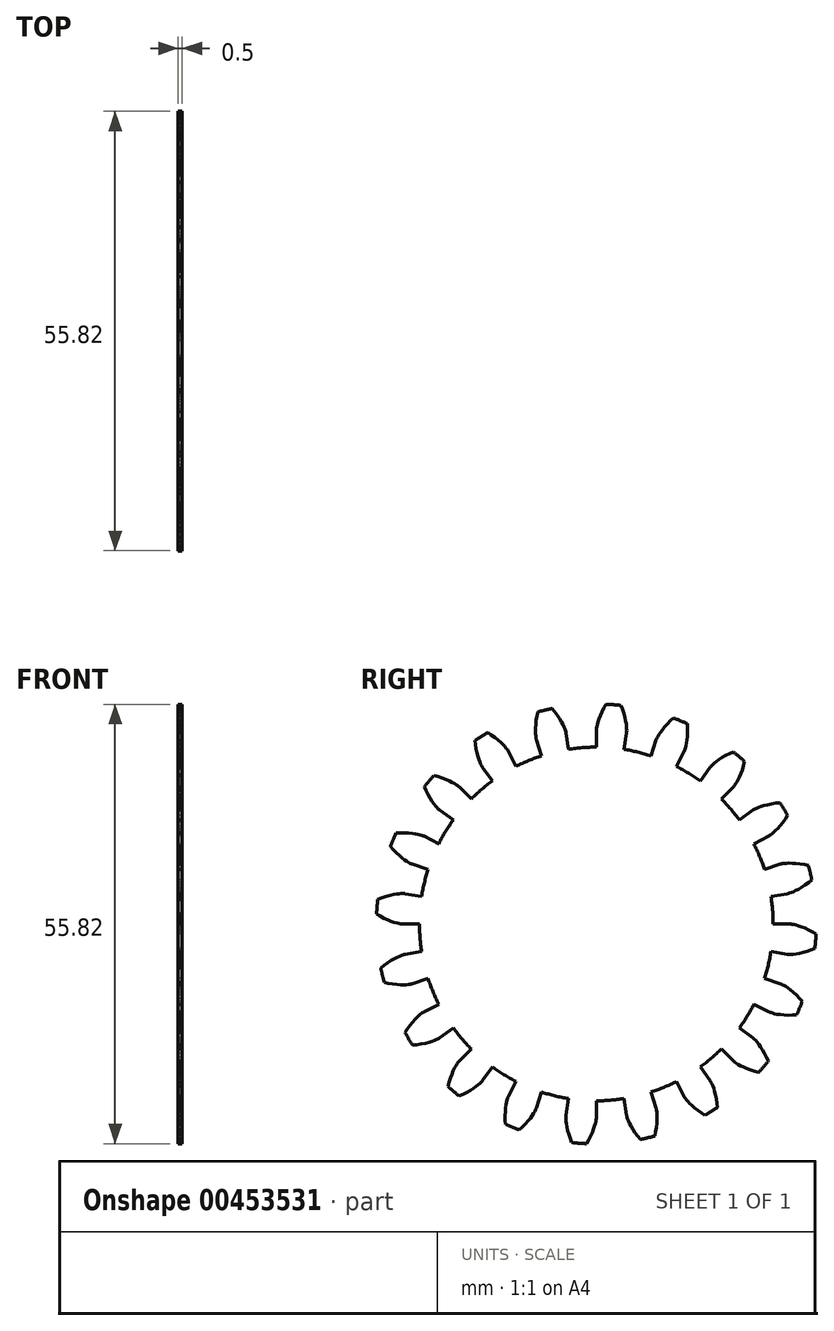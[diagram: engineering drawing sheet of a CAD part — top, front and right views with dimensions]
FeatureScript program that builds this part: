
annotation { "Feature Type Name" : "Feature", "Feature Type Description" : "" }
export const myFeature = defineFeature(function(context is Context, id is Id, definition is map)
    precondition{}
    {
        {
            assignVariable(context, id + "F0", {"name" : "GearThickness", "anyValue" : .5});
        }
        {
            var Q0;
            Q0=qCreatedBy(makeId("Right.planeOp"),FACE);
            var sketch = newSketch(context, id + "F1", { "sketchPlane" : qUnion([Q0])});
            skCircle(sketch, "E0", {"center": v(0, 0) * mm, "radius": 22.46 * mm});
            skCircle(sketch, "E1", {"center": v(0, 0) * mm, "radius": 24.6 * mm, "construction": true});
            skCircle(sketch, "E2", {"center": v(0, 0) * mm, "radius": 25.4 * mm, "construction": true});
            skCircle(sketch, "E3", {"center": v(0, 0) * mm, "radius": 27.94 * mm});
            skLineSegment(sketch, "E4", {"start": v(0, 0) * mm, "end": v(-24.6, 0) * mm, "construction": true});
            skLineSegment(sketch, "E5.1.0", {"start": v(0, 0) * mm, "end": v(-24.56, 1.23) * mm, "construction": true});
            skLineSegment(sketch, "E5.2.0", {"start": v(0, 0) * mm, "end": v(-24.47, 2.45) * mm, "construction": true});
            skLineSegment(sketch, "E5.3.0", {"start": v(0, 0) * mm, "end": v(-24.31, 3.67) * mm, "construction": true});
            skLineSegment(sketch, "E5.4.0", {"start": v(0, 0) * mm, "end": v(-24.1, 4.89) * mm, "construction": true});
            skLineSegment(sketch, "E5.5.0", {"start": v(0, 0) * mm, "end": v(-23.83, 6.08) * mm, "construction": true});
            skLineSegment(sketch, "E5.6.0", {"start": v(0, 0) * mm, "end": v(-23.5, 7.27) * mm, "construction": true});
            skLineSegment(sketch, "E5.7.0", {"start": v(0, 0) * mm, "end": v(-23.1, 8.43) * mm, "construction": true});
            skLineSegment(sketch, "E5.8.0", {"start": v(0, 0) * mm, "end": v(-22.65, 9.58) * mm, "construction": true});
            skLineSegment(sketch, "E5.9.0", {"start": v(0, 0) * mm, "end": v(-22.14, 10.7) * mm, "construction": true});
            skLineSegment(sketch, "E5.10.0", {"start": v(0, 0) * mm, "end": v(-21.58, 11.79) * mm, "construction": true});
            skLineSegment(sketch, "E5.11.0", {"start": v(0, 0) * mm, "end": v(-20.96, 12.85) * mm, "construction": true});
            skLineSegment(sketch, "E5.12.0", {"start": v(0, 0) * mm, "end": v(-20.3, 13.89) * mm, "construction": true});
            skLineSegment(sketch, "E5.13.0", {"start": v(0, 0) * mm, "end": v(-19.58, 14.88) * mm, "construction": true});
            skLineSegment(sketch, "E5.14.0", {"start": v(0, 0) * mm, "end": v(-18.8, 15.84) * mm, "construction": true});
            skLineSegment(sketch, "E5.anchor2", {"start": v(0, 0) * mm, "end": v(-18.8, 15.84) * mm, "construction": true});
            skLineSegment(sketch, "E6", {"start": v(-24.56, 1.23) * mm, "end": v(-24.62, 0) * mm, "construction": true});
            skLineSegment(sketch, "E7", {"start": v(-24.47, 2.45) * mm, "end": v(-24.71, 0) * mm, "construction": true});
            skLineSegment(sketch, "E8", {"start": v(-24.31, 3.67) * mm, "end": v(-24.87, 0.03) * mm, "construction": true});
            skLineSegment(sketch, "E9", {"start": v(-23.83, 6.08) * mm, "end": v(-25.35, 0.13) * mm, "construction": true});
            skLineSegment(sketch, "E10", {"start": v(-23.5, 7.27) * mm, "end": v(-25.67, 0.22) * mm, "construction": true});
            skLineSegment(sketch, "E11", {"start": v(-23.1, 8.43) * mm, "end": v(-26.05, 0.35) * mm, "construction": true});
            skLineSegment(sketch, "E12", {"start": v(-22.65, 9.58) * mm, "end": v(-26.48, 0.52) * mm, "construction": true});
            skLineSegment(sketch, "E13", {"start": v(-22.14, 10.7) * mm, "end": v(-26.96, 0.73) * mm, "construction": true});
            skLineSegment(sketch, "E14", {"start": v(-21.58, 11.79) * mm, "end": v(-27.48, 1) * mm, "construction": true});
            skLineSegment(sketch, "E15", {"start": v(-20.96, 12.85) * mm, "end": v(-28.03, 1.32) * mm, "construction": true});
            skLineSegment(sketch, "E16", {"start": v(-24.1, 4.89) * mm, "end": v(-25.08, 0.07) * mm, "construction": true});
            skLineSegment(sketch, "E17", {"start": v(-20.3, 13.89) * mm, "end": v(-28.63, 1.7) * mm, "construction": true});
            skLineSegment(sketch, "E18", {"start": v(-19.58, 14.88) * mm, "end": v(-29.25, 2.16) * mm, "construction": true});
            skLineSegment(sketch, "E19", {"start": v(-18.8, 15.84) * mm, "end": v(-29.9, 2.68) * mm, "construction": true});
            skLineSegment(sketch, "E20", {"start": v(0, 0) * mm, "end": v(-24.52, 1.93) * mm, "construction": true});
            skLineSegment(sketch, "E21", {"start": v(-22.46, 0) * mm, "end": v(-24.6, 0) * mm});
            skLineSegment(sketch, "E22.MirrorCS", {"start": v(-22.18, 3.51) * mm, "end": v(-24.29, 3.85) * mm});
            skLineSegment(sketch, "E23", {"start": v(-24.6, 0) * mm, "end": v(-24.62, 0) * mm});
            skLineSegment(sketch, "E24", {"start": v(-24.62, 0) * mm, "end": v(-24.71, 0) * mm});
            skLineSegment(sketch, "E25", {"start": v(-24.71, 0) * mm, "end": v(-24.87, 0.03) * mm});
            skLineSegment(sketch, "E26", {"start": v(-24.87, 0.03) * mm, "end": v(-25.08, 0.07) * mm});
            skLineSegment(sketch, "E27", {"start": v(-25.08, 0.07) * mm, "end": v(-25.35, 0.13) * mm});
            skLineSegment(sketch, "E28", {"start": v(-25.35, 0.13) * mm, "end": v(-25.67, 0.22) * mm});
            skLineSegment(sketch, "E29", {"start": v(-25.67, 0.22) * mm, "end": v(-26.05, 0.35) * mm});
            skLineSegment(sketch, "E30", {"start": v(-26.05, 0.35) * mm, "end": v(-26.48, 0.52) * mm});
            skLineSegment(sketch, "E31", {"start": v(-26.48, 0.52) * mm, "end": v(-26.96, 0.73) * mm});
            skLineSegment(sketch, "E32", {"start": v(-26.96, 0.73) * mm, "end": v(-27.48, 1) * mm});
            skLineSegment(sketch, "E33", {"start": v(-27.48, 1) * mm, "end": v(-28.03, 1.32) * mm});
            skLineSegment(sketch, "E34", {"start": v(-28.03, 1.32) * mm, "end": v(-28.63, 1.7) * mm});
            skLineSegment(sketch, "E35", {"start": v(-28.63, 1.7) * mm, "end": v(-29.25, 2.16) * mm});
            skLineSegment(sketch, "E36", {"start": v(-29.25, 2.16) * mm, "end": v(-29.9, 2.68) * mm});
            skLineSegment(sketch, "E37.MirrorCS", {"start": v(-24.29, 3.85) * mm, "end": v(-24.32, 3.85) * mm});
            skLineSegment(sketch, "E38.MirrorCS", {"start": v(-24.32, 3.85) * mm, "end": v(-24.41, 3.86) * mm});
            skLineSegment(sketch, "E39.MirrorCS", {"start": v(-24.41, 3.86) * mm, "end": v(-24.56, 3.86) * mm});
            skLineSegment(sketch, "E40.MirrorCS", {"start": v(-24.56, 3.86) * mm, "end": v(-24.78, 3.86) * mm});
            skLineSegment(sketch, "E41.MirrorCS", {"start": v(-25.06, 3.84) * mm, "end": v(-25.4, 3.8) * mm});
            skLineSegment(sketch, "E42.MirrorCS", {"start": v(-25.4, 3.8) * mm, "end": v(-25.78, 3.73) * mm});
            skLineSegment(sketch, "E43.MirrorCS", {"start": v(-25.78, 3.73) * mm, "end": v(-26.23, 3.63) * mm});
            skLineSegment(sketch, "E44.MirrorCS", {"start": v(-26.23, 3.63) * mm, "end": v(-26.74, 3.5) * mm});
            skLineSegment(sketch, "E45.MirrorCS", {"start": v(-27.3, 3.31) * mm, "end": v(-27.9, 3.08) * mm});
            skLineSegment(sketch, "E46.MirrorCS", {"start": v(-26.74, 3.5) * mm, "end": v(-27.3, 3.31) * mm});
            skLineSegment(sketch, "E47.MirrorCS", {"start": v(-27.9, 3.08) * mm, "end": v(-28.54, 2.8) * mm});
            skLineSegment(sketch, "E48.MirrorCS", {"start": v(-28.54, 2.8) * mm, "end": v(-29.23, 2.44) * mm});
            skLineSegment(sketch, "E49.MirrorCS", {"start": v(-29.23, 2.44) * mm, "end": v(-29.95, 2.03) * mm});
            skLineSegment(sketch, "E50.MirrorCS", {"start": v(-24.78, 3.86) * mm, "end": v(-25.06, 3.84) * mm});
            skLineSegment(sketch, "E51.1.0", {"start": v(-21.36, -6.94) * mm, "end": v(-23.39, -7.6) * mm});
            skLineSegment(sketch, "E51.1.1", {"start": v(-27.48, -5.7) * mm, "end": v(-28, -6.16) * mm});
            skLineSegment(sketch, "E51.1.2", {"start": v(-22.18, -3.51) * mm, "end": v(-24.29, -3.85) * mm});
            skLineSegment(sketch, "E51.1.3", {"start": v(-26.98, -5.29) * mm, "end": v(-27.48, -5.7) * mm});
            skLineSegment(sketch, "E51.1.4", {"start": v(-26.44, -7.54) * mm, "end": v(-27.07, -7.4) * mm});
            skLineSegment(sketch, "E51.1.5", {"start": v(-27.07, -7.4) * mm, "end": v(-27.75, -7.22) * mm});
            skLineSegment(sketch, "E51.1.6", {"start": v(-26.5, -4.94) * mm, "end": v(-26.98, -5.29) * mm});
            skLineSegment(sketch, "E51.1.7", {"start": v(-28.55, -6.7) * mm, "end": v(-29.11, -7.32) * mm});
            skLineSegment(sketch, "E51.1.8", {"start": v(-26.07, -4.65) * mm, "end": v(-26.5, -4.94) * mm});
            skLineSegment(sketch, "E51.1.9", {"start": v(-28.48, -6.99) * mm, "end": v(-29.26, -6.7) * mm});
            skLineSegment(sketch, "E51.1.10", {"start": v(-28, -6.16) * mm, "end": v(-28.55, -6.7) * mm});
            skLineSegment(sketch, "E51.1.11", {"start": v(-25.86, -7.63) * mm, "end": v(-26.44, -7.54) * mm});
            skLineSegment(sketch, "E51.1.12", {"start": v(-27.75, -7.22) * mm, "end": v(-28.48, -6.99) * mm});
            skLineSegment(sketch, "E51.1.13", {"start": v(-25.02, -4.1) * mm, "end": v(-25.32, -4.23) * mm});
            skLineSegment(sketch, "E51.1.14", {"start": v(-25.32, -4.23) * mm, "end": v(-25.68, -4.42) * mm});
            skLineSegment(sketch, "E51.1.15", {"start": v(-25.68, -4.42) * mm, "end": v(-26.07, -4.65) * mm});
            skLineSegment(sketch, "E51.1.16", {"start": v(-24.88, -7.72) * mm, "end": v(-25.34, -7.7) * mm});
            skLineSegment(sketch, "E51.1.17", {"start": v(-24.48, -7.72) * mm, "end": v(-24.88, -7.72) * mm});
            skLineSegment(sketch, "E51.1.18", {"start": v(-25.34, -7.7) * mm, "end": v(-25.86, -7.63) * mm});
            skLineSegment(sketch, "E51.1.19", {"start": v(-24.76, -3.99) * mm, "end": v(-25.02, -4.1) * mm});
            skLineSegment(sketch, "E51.1.20", {"start": v(-24.56, -3.92) * mm, "end": v(-24.76, -3.99) * mm});
            skLineSegment(sketch, "E51.1.21", {"start": v(-24.15, -7.71) * mm, "end": v(-24.48, -7.72) * mm});
            skLineSegment(sketch, "E51.1.22", {"start": v(-23.87, -7.69) * mm, "end": v(-24.15, -7.71) * mm});
            skLineSegment(sketch, "E51.1.23", {"start": v(-23.5, -7.63) * mm, "end": v(-23.66, -7.66) * mm});
            skLineSegment(sketch, "E51.1.24", {"start": v(-24.29, -3.85) * mm, "end": v(-24.32, -3.85) * mm});
            skLineSegment(sketch, "E51.1.25", {"start": v(-24.32, -3.85) * mm, "end": v(-24.4, -3.87) * mm});
            skLineSegment(sketch, "E51.1.26", {"start": v(-23.66, -7.66) * mm, "end": v(-23.87, -7.69) * mm});
            skLineSegment(sketch, "E51.1.27", {"start": v(-24.4, -3.87) * mm, "end": v(-24.56, -3.92) * mm});
            skLineSegment(sketch, "E51.1.28", {"start": v(-23.42, -7.6) * mm, "end": v(-23.5, -7.63) * mm});
            skLineSegment(sketch, "E51.1.29", {"start": v(-23.39, -7.6) * mm, "end": v(-23.42, -7.6) * mm});
            skLineSegment(sketch, "E51.2.0", {"start": v(-18.17, -13.2) * mm, "end": v(-19.9, -14.45) * mm});
            skLineSegment(sketch, "E51.2.1", {"start": v(-24.38, -13.9) * mm, "end": v(-24.73, -14.52) * mm});
            skLineSegment(sketch, "E51.2.2", {"start": v(-20.01, -10.2) * mm, "end": v(-21.91, -11.16) * mm});
            skLineSegment(sketch, "E51.2.3", {"start": v(-24.03, -13.36) * mm, "end": v(-24.38, -13.9) * mm});
            skLineSegment(sketch, "E51.2.4", {"start": v(-22.82, -15.34) * mm, "end": v(-23.46, -15.4) * mm});
            skLineSegment(sketch, "E51.2.5", {"start": v(-23.46, -15.4) * mm, "end": v(-24.16, -15.44) * mm});
            skLineSegment(sketch, "E51.2.6", {"start": v(-23.69, -12.89) * mm, "end": v(-24.03, -13.36) * mm});
            skLineSegment(sketch, "E51.2.7", {"start": v(-25.08, -15.2) * mm, "end": v(-25.42, -15.96) * mm});
            skLineSegment(sketch, "E51.2.8", {"start": v(-23.36, -12.48) * mm, "end": v(-23.69, -12.89) * mm});
            skLineSegment(sketch, "E51.2.9", {"start": v(-24.93, -15.45) * mm, "end": v(-25.76, -15.4) * mm});
            skLineSegment(sketch, "E51.2.10", {"start": v(-24.73, -14.52) * mm, "end": v(-25.08, -15.2) * mm});
            skLineSegment(sketch, "E51.2.11", {"start": v(-22.24, -15.25) * mm, "end": v(-22.82, -15.34) * mm});
            skLineSegment(sketch, "E51.2.12", {"start": v(-24.16, -15.44) * mm, "end": v(-24.93, -15.45) * mm});
            skLineSegment(sketch, "E51.2.13", {"start": v(-22.53, -11.62) * mm, "end": v(-22.78, -11.85) * mm});
            skLineSegment(sketch, "E51.2.14", {"start": v(-22.78, -11.85) * mm, "end": v(-23.05, -12.14) * mm});
            skLineSegment(sketch, "E51.2.15", {"start": v(-23.05, -12.14) * mm, "end": v(-23.36, -12.48) * mm});
            skLineSegment(sketch, "E51.2.16", {"start": v(-21.28, -15.03) * mm, "end": v(-21.73, -15.15) * mm});
            skLineSegment(sketch, "E51.2.17", {"start": v(-20.9, -14.91) * mm, "end": v(-21.28, -15.03) * mm});
            skLineSegment(sketch, "E51.2.18", {"start": v(-21.73, -15.15) * mm, "end": v(-22.24, -15.25) * mm});
            skLineSegment(sketch, "E51.2.19", {"start": v(-22.31, -11.44) * mm, "end": v(-22.53, -11.62) * mm});
            skLineSegment(sketch, "E51.2.20", {"start": v(-22.14, -11.31) * mm, "end": v(-22.31, -11.44) * mm});
            skLineSegment(sketch, "E51.2.21", {"start": v(-20.58, -14.8) * mm, "end": v(-20.9, -14.91) * mm});
            skLineSegment(sketch, "E51.2.22", {"start": v(-20.33, -14.69) * mm, "end": v(-20.58, -14.8) * mm});
            skLineSegment(sketch, "E51.2.23", {"start": v(-20, -14.52) * mm, "end": v(-20.13, -14.6) * mm});
            skLineSegment(sketch, "E51.2.24", {"start": v(-21.91, -11.16) * mm, "end": v(-21.94, -11.18) * mm});
            skLineSegment(sketch, "E51.2.25", {"start": v(-21.94, -11.18) * mm, "end": v(-22.02, -11.23) * mm});
            skLineSegment(sketch, "E51.2.26", {"start": v(-20.13, -14.6) * mm, "end": v(-20.33, -14.69) * mm});
            skLineSegment(sketch, "E51.2.27", {"start": v(-22.02, -11.23) * mm, "end": v(-22.14, -11.31) * mm});
            skLineSegment(sketch, "E51.2.28", {"start": v(-19.92, -14.47) * mm, "end": v(-20, -14.52) * mm});
            skLineSegment(sketch, "E51.2.29", {"start": v(-19.9, -14.45) * mm, "end": v(-19.92, -14.47) * mm});
            skLineSegment(sketch, "E51.3.0", {"start": v(-13.2, -18.17) * mm, "end": v(-14.45, -19.9) * mm});
            skLineSegment(sketch, "E51.3.1", {"start": v(-18.89, -20.76) * mm, "end": v(-19.03, -21.45) * mm});
            skLineSegment(sketch, "E51.3.2", {"start": v(-15.88, -15.88) * mm, "end": v(-17.39, -17.39) * mm});
            skLineSegment(sketch, "E51.3.3", {"start": v(-18.72, -20.13) * mm, "end": v(-18.89, -20.76) * mm});
            skLineSegment(sketch, "E51.3.4", {"start": v(-16.96, -21.64) * mm, "end": v(-17.55, -21.9) * mm});
            skLineSegment(sketch, "E51.3.5", {"start": v(-17.55, -21.9) * mm, "end": v(-18.2, -22.16) * mm});
            skLineSegment(sketch, "E51.3.6", {"start": v(-18.54, -19.58) * mm, "end": v(-18.72, -20.13) * mm});
            skLineSegment(sketch, "E51.3.7", {"start": v(-19.16, -22.2) * mm, "end": v(-19.25, -23.03) * mm});
            skLineSegment(sketch, "E51.3.8", {"start": v(-18.36, -19.09) * mm, "end": v(-18.54, -19.58) * mm});
            skLineSegment(sketch, "E51.3.9", {"start": v(-18.94, -22.4) * mm, "end": v(-19.74, -22.61) * mm});
            skLineSegment(sketch, "E51.3.10", {"start": v(-19.03, -21.45) * mm, "end": v(-19.16, -22.2) * mm});
            skLineSegment(sketch, "E51.3.11", {"start": v(-16.44, -21.38) * mm, "end": v(-16.96, -21.64) * mm});
            skLineSegment(sketch, "E51.3.12", {"start": v(-18.2, -22.16) * mm, "end": v(-18.94, -22.4) * mm});
            skLineSegment(sketch, "E51.3.13", {"start": v(-17.83, -18.01) * mm, "end": v(-18, -18.3) * mm});
            skLineSegment(sketch, "E51.3.14", {"start": v(-18, -18.3) * mm, "end": v(-18.18, -18.67) * mm});
            skLineSegment(sketch, "E51.3.15", {"start": v(-18.18, -18.67) * mm, "end": v(-18.36, -19.09) * mm});
            skLineSegment(sketch, "E51.3.16", {"start": v(-15.6, -20.87) * mm, "end": v(-15.98, -21.12) * mm});
            skLineSegment(sketch, "E51.3.17", {"start": v(-15.27, -20.64) * mm, "end": v(-15.6, -20.87) * mm});
            skLineSegment(sketch, "E51.3.18", {"start": v(-15.98, -21.12) * mm, "end": v(-16.44, -21.38) * mm});
            skLineSegment(sketch, "E51.3.19", {"start": v(-17.69, -17.78) * mm, "end": v(-17.83, -18.01) * mm});
            skLineSegment(sketch, "E51.3.20", {"start": v(-17.56, -17.6) * mm, "end": v(-17.69, -17.78) * mm});
            skLineSegment(sketch, "E51.3.21", {"start": v(-15, -20.43) * mm, "end": v(-15.27, -20.64) * mm});
            skLineSegment(sketch, "E51.3.22", {"start": v(-14.8, -20.25) * mm, "end": v(-15, -20.43) * mm});
            skLineSegment(sketch, "E51.3.23", {"start": v(-14.53, -19.99) * mm, "end": v(-14.64, -20.1) * mm});
            skLineSegment(sketch, "E51.3.24", {"start": v(-17.39, -17.39) * mm, "end": v(-17.4, -17.41) * mm});
            skLineSegment(sketch, "E51.3.25", {"start": v(-17.4, -17.41) * mm, "end": v(-17.47, -17.48) * mm});
            skLineSegment(sketch, "E51.3.26", {"start": v(-14.64, -20.1) * mm, "end": v(-14.8, -20.25) * mm});
            skLineSegment(sketch, "E51.3.27", {"start": v(-17.47, -17.48) * mm, "end": v(-17.56, -17.6) * mm});
            skLineSegment(sketch, "E51.3.28", {"start": v(-14.47, -19.92) * mm, "end": v(-14.53, -19.99) * mm});
            skLineSegment(sketch, "E51.3.29", {"start": v(-14.45, -19.9) * mm, "end": v(-14.47, -19.92) * mm});
            skLineSegment(sketch, "E51.4.0", {"start": v(-6.94, -21.36) * mm, "end": v(-7.6, -23.39) * mm});
            skLineSegment(sketch, "E51.4.1", {"start": v(-11.55, -25.58) * mm, "end": v(-11.47, -26.28) * mm});
            skLineSegment(sketch, "E51.4.2", {"start": v(-10.2, -20.01) * mm, "end": v(-11.16, -21.91) * mm});
            skLineSegment(sketch, "E51.4.3", {"start": v(-11.58, -24.93) * mm, "end": v(-11.55, -25.58) * mm});
            skLineSegment(sketch, "E51.4.4", {"start": v(-9.44, -25.82) * mm, "end": v(-9.92, -26.25) * mm});
            skLineSegment(sketch, "E51.4.5", {"start": v(-9.92, -26.25) * mm, "end": v(-10.47, -26.7) * mm});
            skLineSegment(sketch, "E51.4.6", {"start": v(-11.59, -24.35) * mm, "end": v(-11.58, -24.93) * mm});
            skLineSegment(sketch, "E51.4.7", {"start": v(-11.36, -27.04) * mm, "end": v(-11.19, -27.85) * mm});
            skLineSegment(sketch, "E51.4.8", {"start": v(-11.56, -23.83) * mm, "end": v(-11.59, -24.35) * mm});
            skLineSegment(sketch, "E51.4.9", {"start": v(-11.1, -27.15) * mm, "end": v(-11.78, -27.6) * mm});
            skLineSegment(sketch, "E51.4.10", {"start": v(-11.47, -26.28) * mm, "end": v(-11.36, -27.04) * mm});
            skLineSegment(sketch, "E51.4.11", {"start": v(-9.03, -25.41) * mm, "end": v(-9.44, -25.82) * mm});
            skLineSegment(sketch, "E51.4.12", {"start": v(-10.47, -26.7) * mm, "end": v(-11.1, -27.15) * mm});
            skLineSegment(sketch, "E51.4.13", {"start": v(-11.4, -22.64) * mm, "end": v(-11.46, -22.97) * mm});
            skLineSegment(sketch, "E51.4.14", {"start": v(-11.46, -22.97) * mm, "end": v(-11.52, -23.37) * mm});
            skLineSegment(sketch, "E51.4.15", {"start": v(-11.52, -23.37) * mm, "end": v(-11.56, -23.83) * mm});
            skLineSegment(sketch, "E51.4.16", {"start": v(-8.38, -24.67) * mm, "end": v(-8.67, -25.02) * mm});
            skLineSegment(sketch, "E51.4.17", {"start": v(-8.14, -24.35) * mm, "end": v(-8.38, -24.67) * mm});
            skLineSegment(sketch, "E51.4.18", {"start": v(-8.67, -25.02) * mm, "end": v(-9.03, -25.41) * mm});
            skLineSegment(sketch, "E51.4.19", {"start": v(-11.33, -22.37) * mm, "end": v(-11.4, -22.64) * mm});
            skLineSegment(sketch, "E51.4.20", {"start": v(-11.26, -22.17) * mm, "end": v(-11.33, -22.37) * mm});
            skLineSegment(sketch, "E51.4.21", {"start": v(-7.95, -24.07) * mm, "end": v(-8.14, -24.35) * mm});
            skLineSegment(sketch, "E51.4.22", {"start": v(-7.81, -23.83) * mm, "end": v(-7.95, -24.07) * mm});
            skLineSegment(sketch, "E51.4.23", {"start": v(-7.64, -23.5) * mm, "end": v(-7.71, -23.64) * mm});
            skLineSegment(sketch, "E51.4.24", {"start": v(-11.16, -21.91) * mm, "end": v(-11.18, -21.94) * mm});
            skLineSegment(sketch, "E51.4.25", {"start": v(-11.18, -21.94) * mm, "end": v(-11.21, -22.02) * mm});
            skLineSegment(sketch, "E51.4.26", {"start": v(-7.71, -23.64) * mm, "end": v(-7.81, -23.83) * mm});
            skLineSegment(sketch, "E51.4.27", {"start": v(-11.21, -22.02) * mm, "end": v(-11.26, -22.17) * mm});
            skLineSegment(sketch, "E51.4.28", {"start": v(-7.6, -23.42) * mm, "end": v(-7.64, -23.5) * mm});
            skLineSegment(sketch, "E51.4.29", {"start": v(-7.6, -23.39) * mm, "end": v(-7.6, -23.42) * mm});
            skLineSegment(sketch, "E51.5.0", {"start": v(0, -22.46) * mm, "end": v(0, -24.6) * mm});
            skLineSegment(sketch, "E51.5.1", {"start": v(-3.08, -27.9) * mm, "end": v(-2.8, -28.54) * mm});
            skLineSegment(sketch, "E51.5.2", {"start": v(-3.51, -22.18) * mm, "end": v(-3.85, -24.29) * mm});
            skLineSegment(sketch, "E51.5.3", {"start": v(-3.31, -27.3) * mm, "end": v(-3.08, -27.9) * mm});
            skLineSegment(sketch, "E51.5.4", {"start": v(-1, -27.48) * mm, "end": v(-1.32, -28.03) * mm});
            skLineSegment(sketch, "E51.5.5", {"start": v(-1.32, -28.03) * mm, "end": v(-1.7, -28.63) * mm});
            skLineSegment(sketch, "E51.5.6", {"start": v(-3.5, -26.74) * mm, "end": v(-3.31, -27.3) * mm});
            skLineSegment(sketch, "E51.5.7", {"start": v(-2.44, -29.23) * mm, "end": v(-2.03, -29.95) * mm});
            skLineSegment(sketch, "E51.5.8", {"start": v(-3.63, -26.23) * mm, "end": v(-3.5, -26.74) * mm});
            skLineSegment(sketch, "E51.5.9", {"start": v(-2.16, -29.25) * mm, "end": v(-2.68, -29.9) * mm});
            skLineSegment(sketch, "E51.5.10", {"start": v(-2.8, -28.54) * mm, "end": v(-2.44, -29.23) * mm});
            skLineSegment(sketch, "E51.5.11", {"start": v(-0.73, -26.96) * mm, "end": v(-1, -27.48) * mm});
            skLineSegment(sketch, "E51.5.12", {"start": v(-1.7, -28.63) * mm, "end": v(-2.16, -29.25) * mm});
            skLineSegment(sketch, "E51.5.13", {"start": v(-3.84, -25.06) * mm, "end": v(-3.8, -25.4) * mm});
            skLineSegment(sketch, "E51.5.14", {"start": v(-3.8, -25.4) * mm, "end": v(-3.73, -25.78) * mm});
            skLineSegment(sketch, "E51.5.15", {"start": v(-3.73, -25.78) * mm, "end": v(-3.63, -26.23) * mm});
            skLineSegment(sketch, "E51.5.16", {"start": v(-0.35, -26.05) * mm, "end": v(-0.52, -26.48) * mm});
            skLineSegment(sketch, "E51.5.17", {"start": v(-0.22, -25.67) * mm, "end": v(-0.35, -26.05) * mm});
            skLineSegment(sketch, "E51.5.18", {"start": v(-0.52, -26.48) * mm, "end": v(-0.73, -26.96) * mm});
            skLineSegment(sketch, "E51.5.19", {"start": v(-3.86, -24.78) * mm, "end": v(-3.84, -25.06) * mm});
            skLineSegment(sketch, "E51.5.20", {"start": v(-3.86, -24.56) * mm, "end": v(-3.86, -24.78) * mm});
            skLineSegment(sketch, "E51.5.21", {"start": v(-0.13, -25.35) * mm, "end": v(-0.22, -25.67) * mm});
            skLineSegment(sketch, "E51.5.22", {"start": v(-0.07, -25.08) * mm, "end": v(-0.13, -25.35) * mm});
            skLineSegment(sketch, "E51.5.23", {"start": v(0, -24.71) * mm, "end": v(-0.03, -24.87) * mm});
            skLineSegment(sketch, "E51.5.24", {"start": v(-3.85, -24.29) * mm, "end": v(-3.85, -24.32) * mm});
            skLineSegment(sketch, "E51.5.25", {"start": v(-3.85, -24.32) * mm, "end": v(-3.86, -24.41) * mm});
            skLineSegment(sketch, "E51.5.26", {"start": v(-0.03, -24.87) * mm, "end": v(-0.07, -25.08) * mm});
            skLineSegment(sketch, "E51.5.27", {"start": v(-3.86, -24.41) * mm, "end": v(-3.86, -24.56) * mm});
            skLineSegment(sketch, "E51.5.28", {"start": v(0, -24.62) * mm, "end": v(0, -24.71) * mm});
            skLineSegment(sketch, "E51.5.29", {"start": v(0, -24.6) * mm, "end": v(0, -24.62) * mm});
            skLineSegment(sketch, "E51.6.0", {"start": v(6.94, -21.36) * mm, "end": v(7.6, -23.39) * mm});
            skLineSegment(sketch, "E51.6.1", {"start": v(5.7, -27.48) * mm, "end": v(6.16, -28) * mm});
            skLineSegment(sketch, "E51.6.2", {"start": v(3.51, -22.18) * mm, "end": v(3.85, -24.29) * mm});
            skLineSegment(sketch, "E51.6.3", {"start": v(5.29, -26.98) * mm, "end": v(5.7, -27.48) * mm});
            skLineSegment(sketch, "E51.6.4", {"start": v(7.54, -26.44) * mm, "end": v(7.4, -27.07) * mm});
            skLineSegment(sketch, "E51.6.5", {"start": v(7.4, -27.07) * mm, "end": v(7.22, -27.75) * mm});
            skLineSegment(sketch, "E51.6.6", {"start": v(4.94, -26.5) * mm, "end": v(5.29, -26.98) * mm});
            skLineSegment(sketch, "E51.6.7", {"start": v(6.7, -28.55) * mm, "end": v(7.32, -29.11) * mm});
            skLineSegment(sketch, "E51.6.8", {"start": v(4.65, -26.07) * mm, "end": v(4.94, -26.5) * mm});
            skLineSegment(sketch, "E51.6.9", {"start": v(6.99, -28.48) * mm, "end": v(6.7, -29.26) * mm});
            skLineSegment(sketch, "E51.6.10", {"start": v(6.16, -28) * mm, "end": v(6.7, -28.55) * mm});
            skLineSegment(sketch, "E51.6.11", {"start": v(7.63, -25.86) * mm, "end": v(7.54, -26.44) * mm});
            skLineSegment(sketch, "E51.6.12", {"start": v(7.22, -27.75) * mm, "end": v(6.99, -28.48) * mm});
            skLineSegment(sketch, "E51.6.13", {"start": v(4.1, -25.02) * mm, "end": v(4.23, -25.32) * mm});
            skLineSegment(sketch, "E51.6.14", {"start": v(4.23, -25.32) * mm, "end": v(4.42, -25.68) * mm});
            skLineSegment(sketch, "E51.6.15", {"start": v(4.42, -25.68) * mm, "end": v(4.65, -26.07) * mm});
            skLineSegment(sketch, "E51.6.16", {"start": v(7.72, -24.88) * mm, "end": v(7.7, -25.34) * mm});
            skLineSegment(sketch, "E51.6.17", {"start": v(7.72, -24.48) * mm, "end": v(7.72, -24.88) * mm});
            skLineSegment(sketch, "E51.6.18", {"start": v(7.7, -25.34) * mm, "end": v(7.63, -25.86) * mm});
            skLineSegment(sketch, "E51.6.19", {"start": v(3.99, -24.76) * mm, "end": v(4.1, -25.02) * mm});
            skLineSegment(sketch, "E51.6.20", {"start": v(3.92, -24.56) * mm, "end": v(3.99, -24.76) * mm});
            skLineSegment(sketch, "E51.6.21", {"start": v(7.71, -24.15) * mm, "end": v(7.72, -24.48) * mm});
            skLineSegment(sketch, "E51.6.22", {"start": v(7.69, -23.87) * mm, "end": v(7.71, -24.15) * mm});
            skLineSegment(sketch, "E51.6.23", {"start": v(7.63, -23.5) * mm, "end": v(7.66, -23.66) * mm});
            skLineSegment(sketch, "E51.6.24", {"start": v(3.85, -24.29) * mm, "end": v(3.85, -24.32) * mm});
            skLineSegment(sketch, "E51.6.25", {"start": v(3.85, -24.32) * mm, "end": v(3.87, -24.4) * mm});
            skLineSegment(sketch, "E51.6.26", {"start": v(7.66, -23.66) * mm, "end": v(7.69, -23.87) * mm});
            skLineSegment(sketch, "E51.6.27", {"start": v(3.87, -24.4) * mm, "end": v(3.92, -24.56) * mm});
            skLineSegment(sketch, "E51.6.28", {"start": v(7.6, -23.42) * mm, "end": v(7.63, -23.5) * mm});
            skLineSegment(sketch, "E51.6.29", {"start": v(7.6, -23.39) * mm, "end": v(7.6, -23.42) * mm});
            skLineSegment(sketch, "E51.7.0", {"start": v(13.2, -18.17) * mm, "end": v(14.45, -19.9) * mm});
            skLineSegment(sketch, "E51.7.1", {"start": v(13.9, -24.38) * mm, "end": v(14.52, -24.73) * mm});
            skLineSegment(sketch, "E51.7.2", {"start": v(10.2, -20.01) * mm, "end": v(11.16, -21.91) * mm});
            skLineSegment(sketch, "E51.7.3", {"start": v(13.36, -24.03) * mm, "end": v(13.9, -24.38) * mm});
            skLineSegment(sketch, "E51.7.4", {"start": v(15.34, -22.82) * mm, "end": v(15.4, -23.46) * mm});
            skLineSegment(sketch, "E51.7.5", {"start": v(15.4, -23.46) * mm, "end": v(15.44, -24.16) * mm});
            skLineSegment(sketch, "E51.7.6", {"start": v(12.89, -23.69) * mm, "end": v(13.36, -24.03) * mm});
            skLineSegment(sketch, "E51.7.7", {"start": v(15.2, -25.08) * mm, "end": v(15.96, -25.42) * mm});
            skLineSegment(sketch, "E51.7.8", {"start": v(12.48, -23.36) * mm, "end": v(12.89, -23.69) * mm});
            skLineSegment(sketch, "E51.7.9", {"start": v(15.45, -24.93) * mm, "end": v(15.4, -25.76) * mm});
            skLineSegment(sketch, "E51.7.10", {"start": v(14.52, -24.73) * mm, "end": v(15.2, -25.08) * mm});
            skLineSegment(sketch, "E51.7.11", {"start": v(15.25, -22.24) * mm, "end": v(15.34, -22.82) * mm});
            skLineSegment(sketch, "E51.7.12", {"start": v(15.44, -24.16) * mm, "end": v(15.45, -24.93) * mm});
            skLineSegment(sketch, "E51.7.13", {"start": v(11.62, -22.53) * mm, "end": v(11.85, -22.78) * mm});
            skLineSegment(sketch, "E51.7.14", {"start": v(11.85, -22.78) * mm, "end": v(12.14, -23.05) * mm});
            skLineSegment(sketch, "E51.7.15", {"start": v(12.14, -23.05) * mm, "end": v(12.48, -23.36) * mm});
            skLineSegment(sketch, "E51.7.16", {"start": v(15.03, -21.28) * mm, "end": v(15.15, -21.73) * mm});
            skLineSegment(sketch, "E51.7.17", {"start": v(14.91, -20.9) * mm, "end": v(15.03, -21.28) * mm});
            skLineSegment(sketch, "E51.7.18", {"start": v(15.15, -21.73) * mm, "end": v(15.25, -22.24) * mm});
            skLineSegment(sketch, "E51.7.19", {"start": v(11.44, -22.31) * mm, "end": v(11.62, -22.53) * mm});
            skLineSegment(sketch, "E51.7.20", {"start": v(11.31, -22.14) * mm, "end": v(11.44, -22.31) * mm});
            skLineSegment(sketch, "E51.7.21", {"start": v(14.8, -20.58) * mm, "end": v(14.91, -20.9) * mm});
            skLineSegment(sketch, "E51.7.22", {"start": v(14.69, -20.33) * mm, "end": v(14.8, -20.58) * mm});
            skLineSegment(sketch, "E51.7.23", {"start": v(14.52, -20) * mm, "end": v(14.6, -20.13) * mm});
            skLineSegment(sketch, "E51.7.24", {"start": v(11.16, -21.91) * mm, "end": v(11.18, -21.94) * mm});
            skLineSegment(sketch, "E51.7.25", {"start": v(11.18, -21.94) * mm, "end": v(11.23, -22.02) * mm});
            skLineSegment(sketch, "E51.7.26", {"start": v(14.6, -20.13) * mm, "end": v(14.69, -20.33) * mm});
            skLineSegment(sketch, "E51.7.27", {"start": v(11.23, -22.02) * mm, "end": v(11.31, -22.14) * mm});
            skLineSegment(sketch, "E51.7.28", {"start": v(14.47, -19.92) * mm, "end": v(14.52, -20) * mm});
            skLineSegment(sketch, "E51.7.29", {"start": v(14.45, -19.9) * mm, "end": v(14.47, -19.92) * mm});
            skLineSegment(sketch, "E51.8.0", {"start": v(18.17, -13.2) * mm, "end": v(19.9, -14.45) * mm});
            skLineSegment(sketch, "E51.8.1", {"start": v(20.76, -18.89) * mm, "end": v(21.45, -19.03) * mm});
            skLineSegment(sketch, "E51.8.2", {"start": v(15.88, -15.88) * mm, "end": v(17.39, -17.39) * mm});
            skLineSegment(sketch, "E51.8.3", {"start": v(20.13, -18.72) * mm, "end": v(20.76, -18.89) * mm});
            skLineSegment(sketch, "E51.8.4", {"start": v(21.64, -16.96) * mm, "end": v(21.9, -17.55) * mm});
            skLineSegment(sketch, "E51.8.5", {"start": v(21.9, -17.55) * mm, "end": v(22.16, -18.2) * mm});
            skLineSegment(sketch, "E51.8.6", {"start": v(19.58, -18.54) * mm, "end": v(20.13, -18.72) * mm});
            skLineSegment(sketch, "E51.8.7", {"start": v(22.2, -19.16) * mm, "end": v(23.03, -19.25) * mm});
            skLineSegment(sketch, "E51.8.8", {"start": v(19.09, -18.36) * mm, "end": v(19.58, -18.54) * mm});
            skLineSegment(sketch, "E51.8.9", {"start": v(22.4, -18.94) * mm, "end": v(22.61, -19.74) * mm});
            skLineSegment(sketch, "E51.8.10", {"start": v(21.45, -19.03) * mm, "end": v(22.2, -19.16) * mm});
            skLineSegment(sketch, "E51.8.11", {"start": v(21.38, -16.44) * mm, "end": v(21.64, -16.96) * mm});
            skLineSegment(sketch, "E51.8.12", {"start": v(22.16, -18.2) * mm, "end": v(22.4, -18.94) * mm});
            skLineSegment(sketch, "E51.8.13", {"start": v(18.01, -17.83) * mm, "end": v(18.3, -18) * mm});
            skLineSegment(sketch, "E51.8.14", {"start": v(18.3, -18) * mm, "end": v(18.67, -18.18) * mm});
            skLineSegment(sketch, "E51.8.15", {"start": v(18.67, -18.18) * mm, "end": v(19.09, -18.36) * mm});
            skLineSegment(sketch, "E51.8.16", {"start": v(20.87, -15.6) * mm, "end": v(21.12, -15.98) * mm});
            skLineSegment(sketch, "E51.8.17", {"start": v(20.64, -15.27) * mm, "end": v(20.87, -15.6) * mm});
            skLineSegment(sketch, "E51.8.18", {"start": v(21.12, -15.98) * mm, "end": v(21.38, -16.44) * mm});
            skLineSegment(sketch, "E51.8.19", {"start": v(17.78, -17.69) * mm, "end": v(18.01, -17.83) * mm});
            skLineSegment(sketch, "E51.8.20", {"start": v(17.6, -17.56) * mm, "end": v(17.78, -17.69) * mm});
            skLineSegment(sketch, "E51.8.21", {"start": v(20.43, -15) * mm, "end": v(20.64, -15.27) * mm});
            skLineSegment(sketch, "E51.8.22", {"start": v(20.25, -14.8) * mm, "end": v(20.43, -15) * mm});
            skLineSegment(sketch, "E51.8.23", {"start": v(19.99, -14.53) * mm, "end": v(20.1, -14.64) * mm});
            skLineSegment(sketch, "E51.8.24", {"start": v(17.39, -17.39) * mm, "end": v(17.41, -17.4) * mm});
            skLineSegment(sketch, "E51.8.25", {"start": v(17.41, -17.4) * mm, "end": v(17.48, -17.47) * mm});
            skLineSegment(sketch, "E51.8.26", {"start": v(20.1, -14.64) * mm, "end": v(20.25, -14.8) * mm});
            skLineSegment(sketch, "E51.8.27", {"start": v(17.48, -17.47) * mm, "end": v(17.6, -17.56) * mm});
            skLineSegment(sketch, "E51.8.28", {"start": v(19.92, -14.47) * mm, "end": v(19.99, -14.53) * mm});
            skLineSegment(sketch, "E51.8.29", {"start": v(19.9, -14.45) * mm, "end": v(19.92, -14.47) * mm});
            skLineSegment(sketch, "E51.9.0", {"start": v(21.36, -6.94) * mm, "end": v(23.39, -7.6) * mm});
            skLineSegment(sketch, "E51.9.1", {"start": v(25.58, -11.55) * mm, "end": v(26.28, -11.47) * mm});
            skLineSegment(sketch, "E51.9.2", {"start": v(20.01, -10.2) * mm, "end": v(21.91, -11.16) * mm});
            skLineSegment(sketch, "E51.9.3", {"start": v(24.93, -11.58) * mm, "end": v(25.58, -11.55) * mm});
            skLineSegment(sketch, "E51.9.4", {"start": v(25.82, -9.44) * mm, "end": v(26.25, -9.92) * mm});
            skLineSegment(sketch, "E51.9.5", {"start": v(26.25, -9.92) * mm, "end": v(26.7, -10.47) * mm});
            skLineSegment(sketch, "E51.9.6", {"start": v(24.35, -11.59) * mm, "end": v(24.93, -11.58) * mm});
            skLineSegment(sketch, "E51.9.7", {"start": v(27.04, -11.36) * mm, "end": v(27.85, -11.19) * mm});
            skLineSegment(sketch, "E51.9.8", {"start": v(23.83, -11.56) * mm, "end": v(24.35, -11.59) * mm});
            skLineSegment(sketch, "E51.9.9", {"start": v(27.15, -11.1) * mm, "end": v(27.6, -11.78) * mm});
            skLineSegment(sketch, "E51.9.10", {"start": v(26.28, -11.47) * mm, "end": v(27.04, -11.36) * mm});
            skLineSegment(sketch, "E51.9.11", {"start": v(25.41, -9.03) * mm, "end": v(25.82, -9.44) * mm});
            skLineSegment(sketch, "E51.9.12", {"start": v(26.7, -10.47) * mm, "end": v(27.15, -11.1) * mm});
            skLineSegment(sketch, "E51.9.13", {"start": v(22.64, -11.4) * mm, "end": v(22.97, -11.46) * mm});
            skLineSegment(sketch, "E51.9.14", {"start": v(22.97, -11.46) * mm, "end": v(23.37, -11.52) * mm});
            skLineSegment(sketch, "E51.9.15", {"start": v(23.37, -11.52) * mm, "end": v(23.83, -11.56) * mm});
            skLineSegment(sketch, "E51.9.16", {"start": v(24.67, -8.38) * mm, "end": v(25.02, -8.67) * mm});
            skLineSegment(sketch, "E51.9.17", {"start": v(24.35, -8.14) * mm, "end": v(24.67, -8.38) * mm});
            skLineSegment(sketch, "E51.9.18", {"start": v(25.02, -8.67) * mm, "end": v(25.41, -9.03) * mm});
            skLineSegment(sketch, "E51.9.19", {"start": v(22.37, -11.33) * mm, "end": v(22.64, -11.4) * mm});
            skLineSegment(sketch, "E51.9.20", {"start": v(22.17, -11.26) * mm, "end": v(22.37, -11.33) * mm});
            skLineSegment(sketch, "E51.9.21", {"start": v(24.07, -7.95) * mm, "end": v(24.35, -8.14) * mm});
            skLineSegment(sketch, "E51.9.22", {"start": v(23.83, -7.81) * mm, "end": v(24.07, -7.95) * mm});
            skLineSegment(sketch, "E51.9.23", {"start": v(23.5, -7.64) * mm, "end": v(23.64, -7.71) * mm});
            skLineSegment(sketch, "E51.9.24", {"start": v(21.91, -11.16) * mm, "end": v(21.94, -11.18) * mm});
            skLineSegment(sketch, "E51.9.25", {"start": v(21.94, -11.18) * mm, "end": v(22.02, -11.21) * mm});
            skLineSegment(sketch, "E51.9.26", {"start": v(23.64, -7.71) * mm, "end": v(23.83, -7.81) * mm});
            skLineSegment(sketch, "E51.9.27", {"start": v(22.02, -11.21) * mm, "end": v(22.17, -11.26) * mm});
            skLineSegment(sketch, "E51.9.28", {"start": v(23.42, -7.6) * mm, "end": v(23.5, -7.64) * mm});
            skLineSegment(sketch, "E51.9.29", {"start": v(23.39, -7.6) * mm, "end": v(23.42, -7.6) * mm});
            skLineSegment(sketch, "E51.10.0", {"start": v(22.46, 0) * mm, "end": v(24.6, 0) * mm});
            skLineSegment(sketch, "E51.10.1", {"start": v(27.9, -3.08) * mm, "end": v(28.54, -2.8) * mm});
            skLineSegment(sketch, "E51.10.2", {"start": v(22.18, -3.51) * mm, "end": v(24.29, -3.85) * mm});
            skLineSegment(sketch, "E51.10.3", {"start": v(27.3, -3.31) * mm, "end": v(27.9, -3.08) * mm});
            skLineSegment(sketch, "E51.10.4", {"start": v(27.48, -1) * mm, "end": v(28.03, -1.32) * mm});
            skLineSegment(sketch, "E51.10.5", {"start": v(28.03, -1.32) * mm, "end": v(28.63, -1.7) * mm});
            skLineSegment(sketch, "E51.10.6", {"start": v(26.74, -3.5) * mm, "end": v(27.3, -3.31) * mm});
            skLineSegment(sketch, "E51.10.7", {"start": v(29.23, -2.44) * mm, "end": v(29.95, -2.03) * mm});
            skLineSegment(sketch, "E51.10.8", {"start": v(26.23, -3.63) * mm, "end": v(26.74, -3.5) * mm});
            skLineSegment(sketch, "E51.10.9", {"start": v(29.25, -2.16) * mm, "end": v(29.9, -2.68) * mm});
            skLineSegment(sketch, "E51.10.10", {"start": v(28.54, -2.8) * mm, "end": v(29.23, -2.44) * mm});
            skLineSegment(sketch, "E51.10.11", {"start": v(26.96, -0.73) * mm, "end": v(27.48, -1) * mm});
            skLineSegment(sketch, "E51.10.12", {"start": v(28.63, -1.7) * mm, "end": v(29.25, -2.16) * mm});
            skLineSegment(sketch, "E51.10.13", {"start": v(25.06, -3.84) * mm, "end": v(25.4, -3.8) * mm});
            skLineSegment(sketch, "E51.10.14", {"start": v(25.4, -3.8) * mm, "end": v(25.78, -3.73) * mm});
            skLineSegment(sketch, "E51.10.15", {"start": v(25.78, -3.73) * mm, "end": v(26.23, -3.63) * mm});
            skLineSegment(sketch, "E51.10.16", {"start": v(26.05, -0.35) * mm, "end": v(26.48, -0.52) * mm});
            skLineSegment(sketch, "E51.10.17", {"start": v(25.67, -0.22) * mm, "end": v(26.05, -0.35) * mm});
            skLineSegment(sketch, "E51.10.18", {"start": v(26.48, -0.52) * mm, "end": v(26.96, -0.73) * mm});
            skLineSegment(sketch, "E51.10.19", {"start": v(24.78, -3.86) * mm, "end": v(25.06, -3.84) * mm});
            skLineSegment(sketch, "E51.10.20", {"start": v(24.56, -3.86) * mm, "end": v(24.78, -3.86) * mm});
            skLineSegment(sketch, "E51.10.21", {"start": v(25.35, -0.13) * mm, "end": v(25.67, -0.22) * mm});
            skLineSegment(sketch, "E51.10.22", {"start": v(25.08, -0.07) * mm, "end": v(25.35, -0.13) * mm});
            skLineSegment(sketch, "E51.10.23", {"start": v(24.71, 0) * mm, "end": v(24.87, -0.03) * mm});
            skLineSegment(sketch, "E51.10.24", {"start": v(24.29, -3.85) * mm, "end": v(24.32, -3.85) * mm});
            skLineSegment(sketch, "E51.10.25", {"start": v(24.32, -3.85) * mm, "end": v(24.41, -3.86) * mm});
            skLineSegment(sketch, "E51.10.26", {"start": v(24.87, -0.03) * mm, "end": v(25.08, -0.07) * mm});
            skLineSegment(sketch, "E51.10.27", {"start": v(24.41, -3.86) * mm, "end": v(24.56, -3.86) * mm});
            skLineSegment(sketch, "E51.10.28", {"start": v(24.62, 0) * mm, "end": v(24.71, 0) * mm});
            skLineSegment(sketch, "E51.10.29", {"start": v(24.6, 0) * mm, "end": v(24.62, 0) * mm});
            skLineSegment(sketch, "E51.11.0", {"start": v(21.36, 6.94) * mm, "end": v(23.39, 7.6) * mm});
            skLineSegment(sketch, "E51.11.1", {"start": v(27.48, 5.7) * mm, "end": v(28, 6.16) * mm});
            skLineSegment(sketch, "E51.11.2", {"start": v(22.18, 3.51) * mm, "end": v(24.29, 3.85) * mm});
            skLineSegment(sketch, "E51.11.3", {"start": v(26.98, 5.29) * mm, "end": v(27.48, 5.7) * mm});
            skLineSegment(sketch, "E51.11.4", {"start": v(26.44, 7.54) * mm, "end": v(27.07, 7.4) * mm});
            skLineSegment(sketch, "E51.11.5", {"start": v(27.07, 7.4) * mm, "end": v(27.75, 7.22) * mm});
            skLineSegment(sketch, "E51.11.6", {"start": v(26.5, 4.94) * mm, "end": v(26.98, 5.29) * mm});
            skLineSegment(sketch, "E51.11.7", {"start": v(28.55, 6.7) * mm, "end": v(29.11, 7.32) * mm});
            skLineSegment(sketch, "E51.11.8", {"start": v(26.07, 4.65) * mm, "end": v(26.5, 4.94) * mm});
            skLineSegment(sketch, "E51.11.9", {"start": v(28.48, 6.99) * mm, "end": v(29.26, 6.7) * mm});
            skLineSegment(sketch, "E51.11.10", {"start": v(28, 6.16) * mm, "end": v(28.55, 6.7) * mm});
            skLineSegment(sketch, "E51.11.11", {"start": v(25.86, 7.63) * mm, "end": v(26.44, 7.54) * mm});
            skLineSegment(sketch, "E51.11.12", {"start": v(27.75, 7.22) * mm, "end": v(28.48, 6.99) * mm});
            skLineSegment(sketch, "E51.11.13", {"start": v(25.02, 4.1) * mm, "end": v(25.32, 4.23) * mm});
            skLineSegment(sketch, "E51.11.14", {"start": v(25.32, 4.23) * mm, "end": v(25.68, 4.42) * mm});
            skLineSegment(sketch, "E51.11.15", {"start": v(25.68, 4.42) * mm, "end": v(26.07, 4.65) * mm});
            skLineSegment(sketch, "E51.11.16", {"start": v(24.88, 7.72) * mm, "end": v(25.34, 7.7) * mm});
            skLineSegment(sketch, "E51.11.17", {"start": v(24.48, 7.72) * mm, "end": v(24.88, 7.72) * mm});
            skLineSegment(sketch, "E51.11.18", {"start": v(25.34, 7.7) * mm, "end": v(25.86, 7.63) * mm});
            skLineSegment(sketch, "E51.11.19", {"start": v(24.76, 3.99) * mm, "end": v(25.02, 4.1) * mm});
            skLineSegment(sketch, "E51.11.20", {"start": v(24.56, 3.92) * mm, "end": v(24.76, 3.99) * mm});
            skLineSegment(sketch, "E51.11.21", {"start": v(24.15, 7.71) * mm, "end": v(24.48, 7.72) * mm});
            skLineSegment(sketch, "E51.11.22", {"start": v(23.87, 7.69) * mm, "end": v(24.15, 7.71) * mm});
            skLineSegment(sketch, "E51.11.23", {"start": v(23.5, 7.63) * mm, "end": v(23.66, 7.66) * mm});
            skLineSegment(sketch, "E51.11.24", {"start": v(24.29, 3.85) * mm, "end": v(24.32, 3.85) * mm});
            skLineSegment(sketch, "E51.11.25", {"start": v(24.32, 3.85) * mm, "end": v(24.4, 3.87) * mm});
            skLineSegment(sketch, "E51.11.26", {"start": v(23.66, 7.66) * mm, "end": v(23.87, 7.69) * mm});
            skLineSegment(sketch, "E51.11.27", {"start": v(24.4, 3.87) * mm, "end": v(24.56, 3.92) * mm});
            skLineSegment(sketch, "E51.11.28", {"start": v(23.42, 7.6) * mm, "end": v(23.5, 7.63) * mm});
            skLineSegment(sketch, "E51.11.29", {"start": v(23.39, 7.6) * mm, "end": v(23.42, 7.6) * mm});
            skLineSegment(sketch, "E51.12.0", {"start": v(18.17, 13.2) * mm, "end": v(19.9, 14.45) * mm});
            skLineSegment(sketch, "E51.12.1", {"start": v(24.38, 13.9) * mm, "end": v(24.73, 14.52) * mm});
            skLineSegment(sketch, "E51.12.2", {"start": v(20.01, 10.2) * mm, "end": v(21.91, 11.16) * mm});
            skLineSegment(sketch, "E51.12.3", {"start": v(24.03, 13.36) * mm, "end": v(24.38, 13.9) * mm});
            skLineSegment(sketch, "E51.12.4", {"start": v(22.82, 15.34) * mm, "end": v(23.46, 15.4) * mm});
            skLineSegment(sketch, "E51.12.5", {"start": v(23.46, 15.4) * mm, "end": v(24.16, 15.44) * mm});
            skLineSegment(sketch, "E51.12.6", {"start": v(23.69, 12.89) * mm, "end": v(24.03, 13.36) * mm});
            skLineSegment(sketch, "E51.12.7", {"start": v(25.08, 15.2) * mm, "end": v(25.42, 15.96) * mm});
            skLineSegment(sketch, "E51.12.8", {"start": v(23.36, 12.48) * mm, "end": v(23.69, 12.89) * mm});
            skLineSegment(sketch, "E51.12.9", {"start": v(24.93, 15.45) * mm, "end": v(25.76, 15.4) * mm});
            skLineSegment(sketch, "E51.12.10", {"start": v(24.73, 14.52) * mm, "end": v(25.08, 15.2) * mm});
            skLineSegment(sketch, "E51.12.11", {"start": v(22.24, 15.25) * mm, "end": v(22.82, 15.34) * mm});
            skLineSegment(sketch, "E51.12.12", {"start": v(24.16, 15.44) * mm, "end": v(24.93, 15.45) * mm});
            skLineSegment(sketch, "E51.12.13", {"start": v(22.53, 11.62) * mm, "end": v(22.78, 11.85) * mm});
            skLineSegment(sketch, "E51.12.14", {"start": v(22.78, 11.85) * mm, "end": v(23.05, 12.14) * mm});
            skLineSegment(sketch, "E51.12.15", {"start": v(23.05, 12.14) * mm, "end": v(23.36, 12.48) * mm});
            skLineSegment(sketch, "E51.12.16", {"start": v(21.28, 15.03) * mm, "end": v(21.73, 15.15) * mm});
            skLineSegment(sketch, "E51.12.17", {"start": v(20.9, 14.91) * mm, "end": v(21.28, 15.03) * mm});
            skLineSegment(sketch, "E51.12.18", {"start": v(21.73, 15.15) * mm, "end": v(22.24, 15.25) * mm});
            skLineSegment(sketch, "E51.12.19", {"start": v(22.31, 11.44) * mm, "end": v(22.53, 11.62) * mm});
            skLineSegment(sketch, "E51.12.20", {"start": v(22.14, 11.31) * mm, "end": v(22.31, 11.44) * mm});
            skLineSegment(sketch, "E51.12.21", {"start": v(20.58, 14.8) * mm, "end": v(20.9, 14.91) * mm});
            skLineSegment(sketch, "E51.12.22", {"start": v(20.33, 14.69) * mm, "end": v(20.58, 14.8) * mm});
            skLineSegment(sketch, "E51.12.23", {"start": v(20, 14.52) * mm, "end": v(20.13, 14.6) * mm});
            skLineSegment(sketch, "E51.12.24", {"start": v(21.91, 11.16) * mm, "end": v(21.94, 11.18) * mm});
            skLineSegment(sketch, "E51.12.25", {"start": v(21.94, 11.18) * mm, "end": v(22.02, 11.23) * mm});
            skLineSegment(sketch, "E51.12.26", {"start": v(20.13, 14.6) * mm, "end": v(20.33, 14.69) * mm});
            skLineSegment(sketch, "E51.12.27", {"start": v(22.02, 11.23) * mm, "end": v(22.14, 11.31) * mm});
            skLineSegment(sketch, "E51.12.28", {"start": v(19.92, 14.47) * mm, "end": v(20, 14.52) * mm});
            skLineSegment(sketch, "E51.12.29", {"start": v(19.9, 14.45) * mm, "end": v(19.92, 14.47) * mm});
            skLineSegment(sketch, "E51.13.0", {"start": v(13.2, 18.17) * mm, "end": v(14.45, 19.9) * mm});
            skLineSegment(sketch, "E51.13.1", {"start": v(18.89, 20.76) * mm, "end": v(19.03, 21.45) * mm});
            skLineSegment(sketch, "E51.13.2", {"start": v(15.88, 15.88) * mm, "end": v(17.39, 17.39) * mm});
            skLineSegment(sketch, "E51.13.3", {"start": v(18.72, 20.13) * mm, "end": v(18.89, 20.76) * mm});
            skLineSegment(sketch, "E51.13.4", {"start": v(16.96, 21.64) * mm, "end": v(17.55, 21.9) * mm});
            skLineSegment(sketch, "E51.13.5", {"start": v(17.55, 21.9) * mm, "end": v(18.2, 22.16) * mm});
            skLineSegment(sketch, "E51.13.6", {"start": v(18.54, 19.58) * mm, "end": v(18.72, 20.13) * mm});
            skLineSegment(sketch, "E51.13.7", {"start": v(19.16, 22.2) * mm, "end": v(19.25, 23.03) * mm});
            skLineSegment(sketch, "E51.13.8", {"start": v(18.36, 19.09) * mm, "end": v(18.54, 19.58) * mm});
            skLineSegment(sketch, "E51.13.9", {"start": v(18.94, 22.4) * mm, "end": v(19.74, 22.61) * mm});
            skLineSegment(sketch, "E51.13.10", {"start": v(19.03, 21.45) * mm, "end": v(19.16, 22.2) * mm});
            skLineSegment(sketch, "E51.13.11", {"start": v(16.44, 21.38) * mm, "end": v(16.96, 21.64) * mm});
            skLineSegment(sketch, "E51.13.12", {"start": v(18.2, 22.16) * mm, "end": v(18.94, 22.4) * mm});
            skLineSegment(sketch, "E51.13.13", {"start": v(17.83, 18.01) * mm, "end": v(18, 18.3) * mm});
            skLineSegment(sketch, "E51.13.14", {"start": v(18, 18.3) * mm, "end": v(18.18, 18.67) * mm});
            skLineSegment(sketch, "E51.13.15", {"start": v(18.18, 18.67) * mm, "end": v(18.36, 19.09) * mm});
            skLineSegment(sketch, "E51.13.16", {"start": v(15.6, 20.87) * mm, "end": v(15.98, 21.12) * mm});
            skLineSegment(sketch, "E51.13.17", {"start": v(15.27, 20.64) * mm, "end": v(15.6, 20.87) * mm});
            skLineSegment(sketch, "E51.13.18", {"start": v(15.98, 21.12) * mm, "end": v(16.44, 21.38) * mm});
            skLineSegment(sketch, "E51.13.19", {"start": v(17.69, 17.78) * mm, "end": v(17.83, 18.01) * mm});
            skLineSegment(sketch, "E51.13.20", {"start": v(17.56, 17.6) * mm, "end": v(17.69, 17.78) * mm});
            skLineSegment(sketch, "E51.13.21", {"start": v(15, 20.43) * mm, "end": v(15.27, 20.64) * mm});
            skLineSegment(sketch, "E51.13.22", {"start": v(14.8, 20.25) * mm, "end": v(15, 20.43) * mm});
            skLineSegment(sketch, "E51.13.23", {"start": v(14.53, 19.99) * mm, "end": v(14.64, 20.1) * mm});
            skLineSegment(sketch, "E51.13.24", {"start": v(17.39, 17.39) * mm, "end": v(17.4, 17.41) * mm});
            skLineSegment(sketch, "E51.13.25", {"start": v(17.4, 17.41) * mm, "end": v(17.47, 17.48) * mm});
            skLineSegment(sketch, "E51.13.26", {"start": v(14.64, 20.1) * mm, "end": v(14.8, 20.25) * mm});
            skLineSegment(sketch, "E51.13.27", {"start": v(17.47, 17.48) * mm, "end": v(17.56, 17.6) * mm});
            skLineSegment(sketch, "E51.13.28", {"start": v(14.47, 19.92) * mm, "end": v(14.53, 19.99) * mm});
            skLineSegment(sketch, "E51.13.29", {"start": v(14.45, 19.9) * mm, "end": v(14.47, 19.92) * mm});
            skLineSegment(sketch, "E51.14.0", {"start": v(6.94, 21.36) * mm, "end": v(7.6, 23.39) * mm});
            skLineSegment(sketch, "E51.14.1", {"start": v(11.55, 25.58) * mm, "end": v(11.47, 26.28) * mm});
            skLineSegment(sketch, "E51.14.2", {"start": v(10.2, 20.01) * mm, "end": v(11.16, 21.91) * mm});
            skLineSegment(sketch, "E51.14.3", {"start": v(11.58, 24.93) * mm, "end": v(11.55, 25.58) * mm});
            skLineSegment(sketch, "E51.14.4", {"start": v(9.44, 25.82) * mm, "end": v(9.92, 26.25) * mm});
            skLineSegment(sketch, "E51.14.5", {"start": v(9.92, 26.25) * mm, "end": v(10.47, 26.7) * mm});
            skLineSegment(sketch, "E51.14.6", {"start": v(11.59, 24.35) * mm, "end": v(11.58, 24.93) * mm});
            skLineSegment(sketch, "E51.14.7", {"start": v(11.36, 27.04) * mm, "end": v(11.19, 27.85) * mm});
            skLineSegment(sketch, "E51.14.8", {"start": v(11.56, 23.83) * mm, "end": v(11.59, 24.35) * mm});
            skLineSegment(sketch, "E51.14.9", {"start": v(11.1, 27.15) * mm, "end": v(11.78, 27.6) * mm});
            skLineSegment(sketch, "E51.14.10", {"start": v(11.47, 26.28) * mm, "end": v(11.36, 27.04) * mm});
            skLineSegment(sketch, "E51.14.11", {"start": v(9.03, 25.41) * mm, "end": v(9.44, 25.82) * mm});
            skLineSegment(sketch, "E51.14.12", {"start": v(10.47, 26.7) * mm, "end": v(11.1, 27.15) * mm});
            skLineSegment(sketch, "E51.14.13", {"start": v(11.4, 22.64) * mm, "end": v(11.46, 22.97) * mm});
            skLineSegment(sketch, "E51.14.14", {"start": v(11.46, 22.97) * mm, "end": v(11.52, 23.37) * mm});
            skLineSegment(sketch, "E51.14.15", {"start": v(11.52, 23.37) * mm, "end": v(11.56, 23.83) * mm});
            skLineSegment(sketch, "E51.14.16", {"start": v(8.38, 24.67) * mm, "end": v(8.67, 25.02) * mm});
            skLineSegment(sketch, "E51.14.17", {"start": v(8.14, 24.35) * mm, "end": v(8.38, 24.67) * mm});
            skLineSegment(sketch, "E51.14.18", {"start": v(8.67, 25.02) * mm, "end": v(9.03, 25.41) * mm});
            skLineSegment(sketch, "E51.14.19", {"start": v(11.33, 22.37) * mm, "end": v(11.4, 22.64) * mm});
            skLineSegment(sketch, "E51.14.20", {"start": v(11.26, 22.17) * mm, "end": v(11.33, 22.37) * mm});
            skLineSegment(sketch, "E51.14.21", {"start": v(7.95, 24.07) * mm, "end": v(8.14, 24.35) * mm});
            skLineSegment(sketch, "E51.14.22", {"start": v(7.81, 23.83) * mm, "end": v(7.95, 24.07) * mm});
            skLineSegment(sketch, "E51.14.23", {"start": v(7.64, 23.5) * mm, "end": v(7.71, 23.64) * mm});
            skLineSegment(sketch, "E51.14.24", {"start": v(11.16, 21.91) * mm, "end": v(11.18, 21.94) * mm});
            skLineSegment(sketch, "E51.14.25", {"start": v(11.18, 21.94) * mm, "end": v(11.21, 22.02) * mm});
            skLineSegment(sketch, "E51.14.26", {"start": v(7.71, 23.64) * mm, "end": v(7.81, 23.83) * mm});
            skLineSegment(sketch, "E51.14.27", {"start": v(11.21, 22.02) * mm, "end": v(11.26, 22.17) * mm});
            skLineSegment(sketch, "E51.14.28", {"start": v(7.6, 23.42) * mm, "end": v(7.64, 23.5) * mm});
            skLineSegment(sketch, "E51.14.29", {"start": v(7.6, 23.39) * mm, "end": v(7.6, 23.42) * mm});
            skLineSegment(sketch, "E51.15.0", {"start": v(0, 22.46) * mm, "end": v(0, 24.6) * mm});
            skLineSegment(sketch, "E51.15.1", {"start": v(3.08, 27.9) * mm, "end": v(2.8, 28.54) * mm});
            skLineSegment(sketch, "E51.15.2", {"start": v(3.51, 22.18) * mm, "end": v(3.85, 24.29) * mm});
            skLineSegment(sketch, "E51.15.3", {"start": v(3.31, 27.3) * mm, "end": v(3.08, 27.9) * mm});
            skLineSegment(sketch, "E51.15.4", {"start": v(1, 27.48) * mm, "end": v(1.32, 28.03) * mm});
            skLineSegment(sketch, "E51.15.5", {"start": v(1.32, 28.03) * mm, "end": v(1.7, 28.63) * mm});
            skLineSegment(sketch, "E51.15.6", {"start": v(3.5, 26.74) * mm, "end": v(3.31, 27.3) * mm});
            skLineSegment(sketch, "E51.15.7", {"start": v(2.44, 29.23) * mm, "end": v(2.03, 29.95) * mm});
            skLineSegment(sketch, "E51.15.8", {"start": v(3.63, 26.23) * mm, "end": v(3.5, 26.74) * mm});
            skLineSegment(sketch, "E51.15.9", {"start": v(2.16, 29.25) * mm, "end": v(2.68, 29.9) * mm});
            skLineSegment(sketch, "E51.15.10", {"start": v(2.8, 28.54) * mm, "end": v(2.44, 29.23) * mm});
            skLineSegment(sketch, "E51.15.11", {"start": v(0.73, 26.96) * mm, "end": v(1, 27.48) * mm});
            skLineSegment(sketch, "E51.15.12", {"start": v(1.7, 28.63) * mm, "end": v(2.16, 29.25) * mm});
            skLineSegment(sketch, "E51.15.13", {"start": v(3.84, 25.06) * mm, "end": v(3.8, 25.4) * mm});
            skLineSegment(sketch, "E51.15.14", {"start": v(3.8, 25.4) * mm, "end": v(3.73, 25.78) * mm});
            skLineSegment(sketch, "E51.15.15", {"start": v(3.73, 25.78) * mm, "end": v(3.63, 26.23) * mm});
            skLineSegment(sketch, "E51.15.16", {"start": v(0.35, 26.05) * mm, "end": v(0.52, 26.48) * mm});
            skLineSegment(sketch, "E51.15.17", {"start": v(0.22, 25.67) * mm, "end": v(0.35, 26.05) * mm});
            skLineSegment(sketch, "E51.15.18", {"start": v(0.52, 26.48) * mm, "end": v(0.73, 26.96) * mm});
            skLineSegment(sketch, "E51.15.19", {"start": v(3.86, 24.78) * mm, "end": v(3.84, 25.06) * mm});
            skLineSegment(sketch, "E51.15.20", {"start": v(3.86, 24.56) * mm, "end": v(3.86, 24.78) * mm});
            skLineSegment(sketch, "E51.15.21", {"start": v(0.13, 25.35) * mm, "end": v(0.22, 25.67) * mm});
            skLineSegment(sketch, "E51.15.22", {"start": v(0.07, 25.08) * mm, "end": v(0.13, 25.35) * mm});
            skLineSegment(sketch, "E51.15.23", {"start": v(0, 24.71) * mm, "end": v(0.03, 24.87) * mm});
            skLineSegment(sketch, "E51.15.24", {"start": v(3.85, 24.29) * mm, "end": v(3.85, 24.32) * mm});
            skLineSegment(sketch, "E51.15.25", {"start": v(3.85, 24.32) * mm, "end": v(3.86, 24.41) * mm});
            skLineSegment(sketch, "E51.15.26", {"start": v(0.03, 24.87) * mm, "end": v(0.07, 25.08) * mm});
            skLineSegment(sketch, "E51.15.27", {"start": v(3.86, 24.41) * mm, "end": v(3.86, 24.56) * mm});
            skLineSegment(sketch, "E51.15.28", {"start": v(0, 24.62) * mm, "end": v(0, 24.71) * mm});
            skLineSegment(sketch, "E51.15.29", {"start": v(0, 24.6) * mm, "end": v(0, 24.62) * mm});
            skLineSegment(sketch, "E51.16.0", {"start": v(-6.94, 21.36) * mm, "end": v(-7.6, 23.39) * mm});
            skLineSegment(sketch, "E51.16.1", {"start": v(-5.7, 27.48) * mm, "end": v(-6.16, 28) * mm});
            skLineSegment(sketch, "E51.16.2", {"start": v(-3.51, 22.18) * mm, "end": v(-3.85, 24.29) * mm});
            skLineSegment(sketch, "E51.16.3", {"start": v(-5.29, 26.98) * mm, "end": v(-5.7, 27.48) * mm});
            skLineSegment(sketch, "E51.16.4", {"start": v(-7.54, 26.44) * mm, "end": v(-7.4, 27.07) * mm});
            skLineSegment(sketch, "E51.16.5", {"start": v(-7.4, 27.07) * mm, "end": v(-7.22, 27.75) * mm});
            skLineSegment(sketch, "E51.16.6", {"start": v(-4.94, 26.5) * mm, "end": v(-5.29, 26.98) * mm});
            skLineSegment(sketch, "E51.16.7", {"start": v(-6.7, 28.55) * mm, "end": v(-7.32, 29.11) * mm});
            skLineSegment(sketch, "E51.16.8", {"start": v(-4.65, 26.07) * mm, "end": v(-4.94, 26.5) * mm});
            skLineSegment(sketch, "E51.16.9", {"start": v(-6.99, 28.48) * mm, "end": v(-6.7, 29.26) * mm});
            skLineSegment(sketch, "E51.16.10", {"start": v(-6.16, 28) * mm, "end": v(-6.7, 28.55) * mm});
            skLineSegment(sketch, "E51.16.11", {"start": v(-7.63, 25.86) * mm, "end": v(-7.54, 26.44) * mm});
            skLineSegment(sketch, "E51.16.12", {"start": v(-7.22, 27.75) * mm, "end": v(-6.99, 28.48) * mm});
            skLineSegment(sketch, "E51.16.13", {"start": v(-4.1, 25.02) * mm, "end": v(-4.23, 25.32) * mm});
            skLineSegment(sketch, "E51.16.14", {"start": v(-4.23, 25.32) * mm, "end": v(-4.42, 25.68) * mm});
            skLineSegment(sketch, "E51.16.15", {"start": v(-4.42, 25.68) * mm, "end": v(-4.65, 26.07) * mm});
            skLineSegment(sketch, "E51.16.16", {"start": v(-7.72, 24.88) * mm, "end": v(-7.7, 25.34) * mm});
            skLineSegment(sketch, "E51.16.17", {"start": v(-7.72, 24.48) * mm, "end": v(-7.72, 24.88) * mm});
            skLineSegment(sketch, "E51.16.18", {"start": v(-7.7, 25.34) * mm, "end": v(-7.63, 25.86) * mm});
            skLineSegment(sketch, "E51.16.19", {"start": v(-3.99, 24.76) * mm, "end": v(-4.1, 25.02) * mm});
            skLineSegment(sketch, "E51.16.20", {"start": v(-3.92, 24.56) * mm, "end": v(-3.99, 24.76) * mm});
            skLineSegment(sketch, "E51.16.21", {"start": v(-7.71, 24.15) * mm, "end": v(-7.72, 24.48) * mm});
            skLineSegment(sketch, "E51.16.22", {"start": v(-7.69, 23.87) * mm, "end": v(-7.71, 24.15) * mm});
            skLineSegment(sketch, "E51.16.23", {"start": v(-7.63, 23.5) * mm, "end": v(-7.66, 23.66) * mm});
            skLineSegment(sketch, "E51.16.24", {"start": v(-3.85, 24.29) * mm, "end": v(-3.85, 24.32) * mm});
            skLineSegment(sketch, "E51.16.25", {"start": v(-3.85, 24.32) * mm, "end": v(-3.87, 24.4) * mm});
            skLineSegment(sketch, "E51.16.26", {"start": v(-7.66, 23.66) * mm, "end": v(-7.69, 23.87) * mm});
            skLineSegment(sketch, "E51.16.27", {"start": v(-3.87, 24.4) * mm, "end": v(-3.92, 24.56) * mm});
            skLineSegment(sketch, "E51.16.28", {"start": v(-7.6, 23.42) * mm, "end": v(-7.63, 23.5) * mm});
            skLineSegment(sketch, "E51.16.29", {"start": v(-7.6, 23.39) * mm, "end": v(-7.6, 23.42) * mm});
            skLineSegment(sketch, "E51.17.0", {"start": v(-13.2, 18.17) * mm, "end": v(-14.45, 19.9) * mm});
            skLineSegment(sketch, "E51.17.1", {"start": v(-13.9, 24.38) * mm, "end": v(-14.52, 24.73) * mm});
            skLineSegment(sketch, "E51.17.2", {"start": v(-10.2, 20.01) * mm, "end": v(-11.16, 21.91) * mm});
            skLineSegment(sketch, "E51.17.3", {"start": v(-13.36, 24.03) * mm, "end": v(-13.9, 24.38) * mm});
            skLineSegment(sketch, "E51.17.4", {"start": v(-15.34, 22.82) * mm, "end": v(-15.4, 23.46) * mm});
            skLineSegment(sketch, "E51.17.5", {"start": v(-15.4, 23.46) * mm, "end": v(-15.44, 24.16) * mm});
            skLineSegment(sketch, "E51.17.6", {"start": v(-12.89, 23.69) * mm, "end": v(-13.36, 24.03) * mm});
            skLineSegment(sketch, "E51.17.7", {"start": v(-15.2, 25.08) * mm, "end": v(-15.96, 25.42) * mm});
            skLineSegment(sketch, "E51.17.8", {"start": v(-12.48, 23.36) * mm, "end": v(-12.89, 23.69) * mm});
            skLineSegment(sketch, "E51.17.9", {"start": v(-15.45, 24.93) * mm, "end": v(-15.4, 25.76) * mm});
            skLineSegment(sketch, "E51.17.10", {"start": v(-14.52, 24.73) * mm, "end": v(-15.2, 25.08) * mm});
            skLineSegment(sketch, "E51.17.11", {"start": v(-15.25, 22.24) * mm, "end": v(-15.34, 22.82) * mm});
            skLineSegment(sketch, "E51.17.12", {"start": v(-15.44, 24.16) * mm, "end": v(-15.45, 24.93) * mm});
            skLineSegment(sketch, "E51.17.13", {"start": v(-11.62, 22.53) * mm, "end": v(-11.85, 22.78) * mm});
            skLineSegment(sketch, "E51.17.14", {"start": v(-11.85, 22.78) * mm, "end": v(-12.14, 23.05) * mm});
            skLineSegment(sketch, "E51.17.15", {"start": v(-12.14, 23.05) * mm, "end": v(-12.48, 23.36) * mm});
            skLineSegment(sketch, "E51.17.16", {"start": v(-15.03, 21.28) * mm, "end": v(-15.15, 21.73) * mm});
            skLineSegment(sketch, "E51.17.17", {"start": v(-14.91, 20.9) * mm, "end": v(-15.03, 21.28) * mm});
            skLineSegment(sketch, "E51.17.18", {"start": v(-15.15, 21.73) * mm, "end": v(-15.25, 22.24) * mm});
            skLineSegment(sketch, "E51.17.19", {"start": v(-11.44, 22.31) * mm, "end": v(-11.62, 22.53) * mm});
            skLineSegment(sketch, "E51.17.20", {"start": v(-11.31, 22.14) * mm, "end": v(-11.44, 22.31) * mm});
            skLineSegment(sketch, "E51.17.21", {"start": v(-14.8, 20.58) * mm, "end": v(-14.91, 20.9) * mm});
            skLineSegment(sketch, "E51.17.22", {"start": v(-14.69, 20.33) * mm, "end": v(-14.8, 20.58) * mm});
            skLineSegment(sketch, "E51.17.23", {"start": v(-14.52, 20) * mm, "end": v(-14.6, 20.13) * mm});
            skLineSegment(sketch, "E51.17.24", {"start": v(-11.16, 21.91) * mm, "end": v(-11.18, 21.94) * mm});
            skLineSegment(sketch, "E51.17.25", {"start": v(-11.18, 21.94) * mm, "end": v(-11.23, 22.02) * mm});
            skLineSegment(sketch, "E51.17.26", {"start": v(-14.6, 20.13) * mm, "end": v(-14.69, 20.33) * mm});
            skLineSegment(sketch, "E51.17.27", {"start": v(-11.23, 22.02) * mm, "end": v(-11.31, 22.14) * mm});
            skLineSegment(sketch, "E51.17.28", {"start": v(-14.47, 19.92) * mm, "end": v(-14.52, 20) * mm});
            skLineSegment(sketch, "E51.17.29", {"start": v(-14.45, 19.9) * mm, "end": v(-14.47, 19.92) * mm});
            skLineSegment(sketch, "E51.18.0", {"start": v(-18.17, 13.2) * mm, "end": v(-19.9, 14.45) * mm});
            skLineSegment(sketch, "E51.18.1", {"start": v(-20.76, 18.89) * mm, "end": v(-21.45, 19.03) * mm});
            skLineSegment(sketch, "E51.18.2", {"start": v(-15.88, 15.88) * mm, "end": v(-17.39, 17.39) * mm});
            skLineSegment(sketch, "E51.18.3", {"start": v(-20.13, 18.72) * mm, "end": v(-20.76, 18.89) * mm});
            skLineSegment(sketch, "E51.18.4", {"start": v(-21.64, 16.96) * mm, "end": v(-21.9, 17.55) * mm});
            skLineSegment(sketch, "E51.18.5", {"start": v(-21.9, 17.55) * mm, "end": v(-22.16, 18.2) * mm});
            skLineSegment(sketch, "E51.18.6", {"start": v(-19.58, 18.54) * mm, "end": v(-20.13, 18.72) * mm});
            skLineSegment(sketch, "E51.18.7", {"start": v(-22.2, 19.16) * mm, "end": v(-23.03, 19.25) * mm});
            skLineSegment(sketch, "E51.18.8", {"start": v(-19.09, 18.36) * mm, "end": v(-19.58, 18.54) * mm});
            skLineSegment(sketch, "E51.18.9", {"start": v(-22.4, 18.94) * mm, "end": v(-22.61, 19.74) * mm});
            skLineSegment(sketch, "E51.18.10", {"start": v(-21.45, 19.03) * mm, "end": v(-22.2, 19.16) * mm});
            skLineSegment(sketch, "E51.18.11", {"start": v(-21.38, 16.44) * mm, "end": v(-21.64, 16.96) * mm});
            skLineSegment(sketch, "E51.18.12", {"start": v(-22.16, 18.2) * mm, "end": v(-22.4, 18.94) * mm});
            skLineSegment(sketch, "E51.18.13", {"start": v(-18.01, 17.83) * mm, "end": v(-18.3, 18) * mm});
            skLineSegment(sketch, "E51.18.14", {"start": v(-18.3, 18) * mm, "end": v(-18.67, 18.18) * mm});
            skLineSegment(sketch, "E51.18.15", {"start": v(-18.67, 18.18) * mm, "end": v(-19.09, 18.36) * mm});
            skLineSegment(sketch, "E51.18.16", {"start": v(-20.87, 15.6) * mm, "end": v(-21.12, 15.98) * mm});
            skLineSegment(sketch, "E51.18.17", {"start": v(-20.64, 15.27) * mm, "end": v(-20.87, 15.6) * mm});
            skLineSegment(sketch, "E51.18.18", {"start": v(-21.12, 15.98) * mm, "end": v(-21.38, 16.44) * mm});
            skLineSegment(sketch, "E51.18.19", {"start": v(-17.78, 17.69) * mm, "end": v(-18.01, 17.83) * mm});
            skLineSegment(sketch, "E51.18.20", {"start": v(-17.6, 17.56) * mm, "end": v(-17.78, 17.69) * mm});
            skLineSegment(sketch, "E51.18.21", {"start": v(-20.43, 15) * mm, "end": v(-20.64, 15.27) * mm});
            skLineSegment(sketch, "E51.18.22", {"start": v(-20.25, 14.8) * mm, "end": v(-20.43, 15) * mm});
            skLineSegment(sketch, "E51.18.23", {"start": v(-19.99, 14.53) * mm, "end": v(-20.1, 14.64) * mm});
            skLineSegment(sketch, "E51.18.24", {"start": v(-17.39, 17.39) * mm, "end": v(-17.41, 17.4) * mm});
            skLineSegment(sketch, "E51.18.25", {"start": v(-17.41, 17.4) * mm, "end": v(-17.48, 17.47) * mm});
            skLineSegment(sketch, "E51.18.26", {"start": v(-20.1, 14.64) * mm, "end": v(-20.25, 14.8) * mm});
            skLineSegment(sketch, "E51.18.27", {"start": v(-17.48, 17.47) * mm, "end": v(-17.6, 17.56) * mm});
            skLineSegment(sketch, "E51.18.28", {"start": v(-19.92, 14.47) * mm, "end": v(-19.99, 14.53) * mm});
            skLineSegment(sketch, "E51.18.29", {"start": v(-19.9, 14.45) * mm, "end": v(-19.92, 14.47) * mm});
            skLineSegment(sketch, "E51.19.0", {"start": v(-21.36, 6.94) * mm, "end": v(-23.39, 7.6) * mm});
            skLineSegment(sketch, "E51.19.1", {"start": v(-25.58, 11.55) * mm, "end": v(-26.28, 11.47) * mm});
            skLineSegment(sketch, "E51.19.2", {"start": v(-20.01, 10.2) * mm, "end": v(-21.91, 11.16) * mm});
            skLineSegment(sketch, "E51.19.3", {"start": v(-24.93, 11.58) * mm, "end": v(-25.58, 11.55) * mm});
            skLineSegment(sketch, "E51.19.4", {"start": v(-25.82, 9.44) * mm, "end": v(-26.25, 9.92) * mm});
            skLineSegment(sketch, "E51.19.5", {"start": v(-26.25, 9.92) * mm, "end": v(-26.7, 10.47) * mm});
            skLineSegment(sketch, "E51.19.6", {"start": v(-24.35, 11.59) * mm, "end": v(-24.93, 11.58) * mm});
            skLineSegment(sketch, "E51.19.7", {"start": v(-27.04, 11.36) * mm, "end": v(-27.85, 11.19) * mm});
            skLineSegment(sketch, "E51.19.8", {"start": v(-23.83, 11.56) * mm, "end": v(-24.35, 11.59) * mm});
            skLineSegment(sketch, "E51.19.9", {"start": v(-27.15, 11.1) * mm, "end": v(-27.6, 11.78) * mm});
            skLineSegment(sketch, "E51.19.10", {"start": v(-26.28, 11.47) * mm, "end": v(-27.04, 11.36) * mm});
            skLineSegment(sketch, "E51.19.11", {"start": v(-25.41, 9.03) * mm, "end": v(-25.82, 9.44) * mm});
            skLineSegment(sketch, "E51.19.12", {"start": v(-26.7, 10.47) * mm, "end": v(-27.15, 11.1) * mm});
            skLineSegment(sketch, "E51.19.13", {"start": v(-22.64, 11.4) * mm, "end": v(-22.97, 11.46) * mm});
            skLineSegment(sketch, "E51.19.14", {"start": v(-22.97, 11.46) * mm, "end": v(-23.37, 11.52) * mm});
            skLineSegment(sketch, "E51.19.15", {"start": v(-23.37, 11.52) * mm, "end": v(-23.83, 11.56) * mm});
            skLineSegment(sketch, "E51.19.16", {"start": v(-24.67, 8.38) * mm, "end": v(-25.02, 8.67) * mm});
            skLineSegment(sketch, "E51.19.17", {"start": v(-24.35, 8.14) * mm, "end": v(-24.67, 8.38) * mm});
            skLineSegment(sketch, "E51.19.18", {"start": v(-25.02, 8.67) * mm, "end": v(-25.41, 9.03) * mm});
            skLineSegment(sketch, "E51.19.19", {"start": v(-22.37, 11.33) * mm, "end": v(-22.64, 11.4) * mm});
            skLineSegment(sketch, "E51.19.20", {"start": v(-22.17, 11.26) * mm, "end": v(-22.37, 11.33) * mm});
            skLineSegment(sketch, "E51.19.21", {"start": v(-24.07, 7.95) * mm, "end": v(-24.35, 8.14) * mm});
            skLineSegment(sketch, "E51.19.22", {"start": v(-23.83, 7.81) * mm, "end": v(-24.07, 7.95) * mm});
            skLineSegment(sketch, "E51.19.23", {"start": v(-23.5, 7.64) * mm, "end": v(-23.64, 7.71) * mm});
            skLineSegment(sketch, "E51.19.24", {"start": v(-21.91, 11.16) * mm, "end": v(-21.94, 11.18) * mm});
            skLineSegment(sketch, "E51.19.25", {"start": v(-21.94, 11.18) * mm, "end": v(-22.02, 11.21) * mm});
            skLineSegment(sketch, "E51.19.26", {"start": v(-23.64, 7.71) * mm, "end": v(-23.83, 7.81) * mm});
            skLineSegment(sketch, "E51.19.27", {"start": v(-22.02, 11.21) * mm, "end": v(-22.17, 11.26) * mm});
            skLineSegment(sketch, "E51.19.28", {"start": v(-23.42, 7.6) * mm, "end": v(-23.5, 7.64) * mm});
            skLineSegment(sketch, "E51.19.29", {"start": v(-23.39, 7.6) * mm, "end": v(-23.42, 7.6) * mm});
            skSolve(sketch);
        }
        {
            var Q0;
            {var subQ0=sQuery(id+"F1.wireOp",EDGE,"E0");var subQ27=makeQuery(id+"F1.imprint","INTERSECT",VERTEX,{"derivedFrom":[subQ0,sQuery(id+"F1.wireOp",EDGE,"E51.10.0")]});Q0=makeQuery(id+"F1.imprint","IMPRINT",FACE,{"disambiguationData":[TD([[makeQuery(id+"F1.imprint","IMPRINT",EDGE,{"disambiguationData":[TD([[subQ27,-1.0]])],"derivedFrom":subQ0}),1.0]])]});}
            var Q1;
            {var subQ0=sQuery(id+"F1.wireOp",EDGE,"E51.1.0");Q1=makeQuery(id+"F1.imprint","IMPRINT",FACE,{"disambiguationData":[TD([[makeQuery(id+"F1.imprint","IMPRINT",EDGE,{"derivedFrom":subQ0}),-1.0]])]});}
            var Q2;
            {var subQ7=sQuery(id+"F1.wireOp",EDGE,"E51.2.0");Q2=makeQuery(id+"F1.imprint","IMPRINT",FACE,{"disambiguationData":[TD([[makeQuery(id+"F1.imprint","IMPRINT",EDGE,{"derivedFrom":subQ7}),-1.0]])]});}
            var Q3;
            {var subQ8=sQuery(id+"F1.wireOp",EDGE,"E51.3.0");Q3=makeQuery(id+"F1.imprint","IMPRINT",FACE,{"disambiguationData":[TD([[makeQuery(id+"F1.imprint","IMPRINT",EDGE,{"derivedFrom":subQ8}),-1.0]])]});}
            var Q4;
            {var subQ2=sQuery(id+"F1.wireOp",EDGE,"E51.4.0");Q4=makeQuery(id+"F1.imprint","IMPRINT",FACE,{"disambiguationData":[TD([[makeQuery(id+"F1.imprint","IMPRINT",EDGE,{"derivedFrom":subQ2}),-1.0]])]});}
            var Q5;
            {var subQ8=sQuery(id+"F1.wireOp",EDGE,"E51.5.0");Q5=makeQuery(id+"F1.imprint","IMPRINT",FACE,{"disambiguationData":[TD([[makeQuery(id+"F1.imprint","IMPRINT",EDGE,{"derivedFrom":subQ8}),-1.0]])]});}
            var Q6;
            {var subQ3=sQuery(id+"F1.wireOp",EDGE,"E51.6.0");Q6=makeQuery(id+"F1.imprint","IMPRINT",FACE,{"disambiguationData":[TD([[makeQuery(id+"F1.imprint","IMPRINT",EDGE,{"derivedFrom":subQ3}),-1.0]])]});}
            var Q7;
            {var subQ0=sQuery(id+"F1.wireOp",EDGE,"E51.7.0");Q7=makeQuery(id+"F1.imprint","IMPRINT",FACE,{"disambiguationData":[TD([[makeQuery(id+"F1.imprint","IMPRINT",EDGE,{"derivedFrom":subQ0}),-1.0]])]});}
            var Q8;
            {var subQ5=sQuery(id+"F1.wireOp",EDGE,"E51.8.0");Q8=makeQuery(id+"F1.imprint","IMPRINT",FACE,{"disambiguationData":[TD([[makeQuery(id+"F1.imprint","IMPRINT",EDGE,{"derivedFrom":subQ5}),-1.0]])]});}
            var Q9;
            {var subQ1=sQuery(id+"F1.wireOp",EDGE,"E51.9.0");Q9=makeQuery(id+"F1.imprint","IMPRINT",FACE,{"disambiguationData":[TD([[makeQuery(id+"F1.imprint","IMPRINT",EDGE,{"derivedFrom":subQ1}),-1.0]])]});}
            var Q10;
            {var subQ5=sQuery(id+"F1.wireOp",EDGE,"E51.10.0");Q10=makeQuery(id+"F1.imprint","IMPRINT",FACE,{"disambiguationData":[TD([[makeQuery(id+"F1.imprint","IMPRINT",EDGE,{"derivedFrom":subQ5}),-1.0]])]});}
            var Q11;
            {var subQ8=sQuery(id+"F1.wireOp",EDGE,"E51.11.0");Q11=makeQuery(id+"F1.imprint","IMPRINT",FACE,{"disambiguationData":[TD([[makeQuery(id+"F1.imprint","IMPRINT",EDGE,{"derivedFrom":subQ8}),-1.0]])]});}
            var Q12;
            {var subQ2=sQuery(id+"F1.wireOp",EDGE,"E51.12.0");Q12=makeQuery(id+"F1.imprint","IMPRINT",FACE,{"disambiguationData":[TD([[makeQuery(id+"F1.imprint","IMPRINT",EDGE,{"derivedFrom":subQ2}),-1.0]])]});}
            var Q13;
            {var subQ3=sQuery(id+"F1.wireOp",EDGE,"E51.13.0");Q13=makeQuery(id+"F1.imprint","IMPRINT",FACE,{"disambiguationData":[TD([[makeQuery(id+"F1.imprint","IMPRINT",EDGE,{"derivedFrom":subQ3}),-1.0]])]});}
            var Q14;
            {var subQ0=sQuery(id+"F1.wireOp",EDGE,"E51.14.0");Q14=makeQuery(id+"F1.imprint","IMPRINT",FACE,{"disambiguationData":[TD([[makeQuery(id+"F1.imprint","IMPRINT",EDGE,{"derivedFrom":subQ0}),-1.0]])]});}
            var Q15;
            {var subQ6=sQuery(id+"F1.wireOp",EDGE,"E51.15.0");Q15=makeQuery(id+"F1.imprint","IMPRINT",FACE,{"disambiguationData":[TD([[makeQuery(id+"F1.imprint","IMPRINT",EDGE,{"derivedFrom":subQ6}),-1.0]])]});}
            var Q16;
            {var subQ5=sQuery(id+"F1.wireOp",EDGE,"E51.16.0");Q16=makeQuery(id+"F1.imprint","IMPRINT",FACE,{"disambiguationData":[TD([[makeQuery(id+"F1.imprint","IMPRINT",EDGE,{"derivedFrom":subQ5}),-1.0]])]});}
            var Q17;
            {var subQ7=sQuery(id+"F1.wireOp",EDGE,"E51.17.0");Q17=makeQuery(id+"F1.imprint","IMPRINT",FACE,{"disambiguationData":[TD([[makeQuery(id+"F1.imprint","IMPRINT",EDGE,{"derivedFrom":subQ7}),-1.0]])]});}
            var Q18;
            {var subQ5=sQuery(id+"F1.wireOp",EDGE,"E51.18.0");Q18=makeQuery(id+"F1.imprint","IMPRINT",FACE,{"disambiguationData":[TD([[makeQuery(id+"F1.imprint","IMPRINT",EDGE,{"derivedFrom":subQ5}),-1.0]])]});}
            var Q19;
            {var subQ8=sQuery(id+"F1.wireOp",EDGE,"E51.19.0");Q19=makeQuery(id+"F1.imprint","IMPRINT",FACE,{"disambiguationData":[TD([[makeQuery(id+"F1.imprint","IMPRINT",EDGE,{"derivedFrom":subQ8}),-1.0]])]});}
            var Q20;
            {var subQ8=sQuery(id+"F1.wireOp",EDGE,"E21");Q20=makeQuery(id+"F1.imprint","IMPRINT",FACE,{"disambiguationData":[TD([[makeQuery(id+"F1.imprint","IMPRINT",EDGE,{"derivedFrom":subQ8}),-1.0]])]});}
            extrude(context, id + "F2", {"entities" : qUnion([Q0, Q1, Q2, Q3, Q4, Q5, Q6, Q7, Q8, Q9, Q10, Q11, Q12, Q13, Q14, Q15, Q16, Q17, Q18, Q19, Q20]), "depth" : (getVariable(context, 'GearThickness')) * mm});
        }
    });
